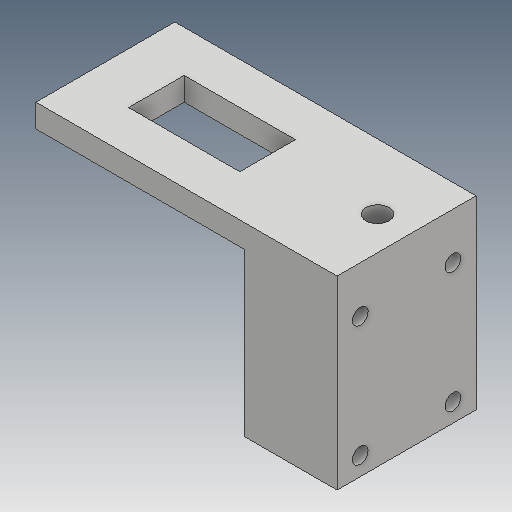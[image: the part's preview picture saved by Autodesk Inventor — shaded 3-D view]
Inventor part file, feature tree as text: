
AUTODESK INVENTOR PART (.ipt)
format: ipt  version: 2018 (Build 220112000, 112)  size: 116,224 bytes
history: native  units: mm
features: sketch x5, other x3
ambient origin geometry x8: Origin, YZ Plane, XZ Plane, XY Plane, X Axis, Y Axis, Z Axis, Center Point
bodies: Volumenkörper1 (feature_tree)
feature tree (8):
  other  "L-Halterung Servo_MIR1.ipt"
  other  "Volumenkörper1::L-Halterung Servo_MIR1.ipt"
  other  "Bezeichnung1"
  sketch  "Skizze1"  dims[d0=10.0mm]
  sketch  "Skizze2"
  sketch  "Skizze3"
  sketch  "Skizze4"
  sketch  "Skizze5"
